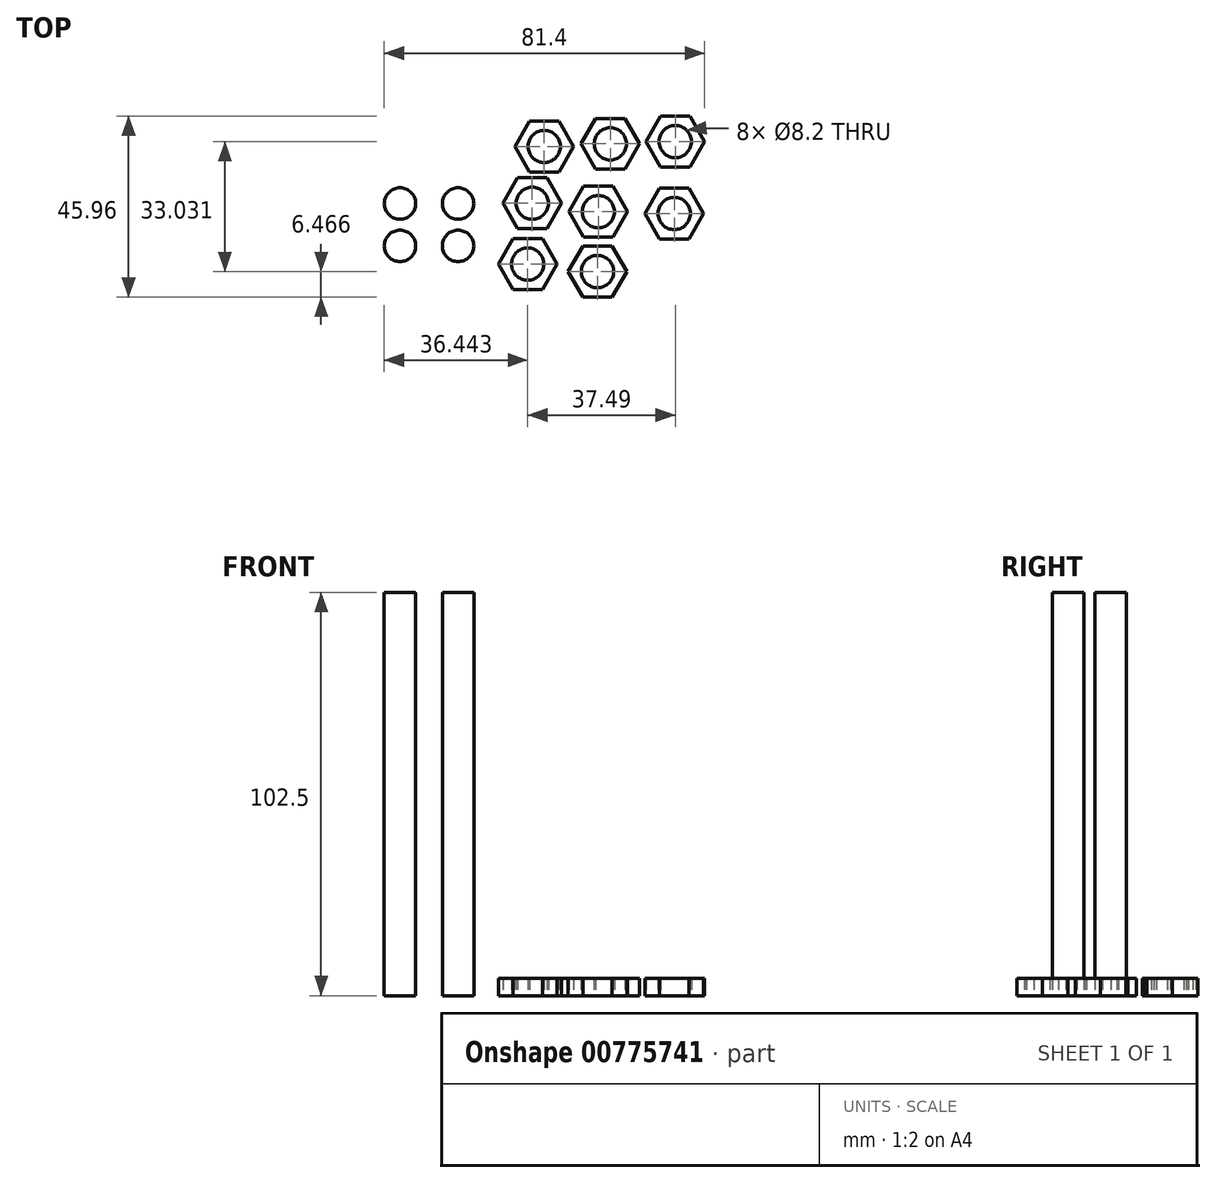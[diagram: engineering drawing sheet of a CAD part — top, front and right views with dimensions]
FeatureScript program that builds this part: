
annotation { "Feature Type Name" : "Feature", "Feature Type Description" : "" }
export const myFeature = defineFeature(function(context is Context, id is Id, definition is map)
    precondition{}
    {
        {
            var Q0;
            Q0=qCreatedBy(makeId("Top.planeOp"),FACE);
            var sketch = newSketch(context, id + "F0", { "sketchPlane" : qUnion([Q0])});
            skCircle(sketch, "E0", {"center": v(-16.12, 12.93) * mm, "radius": 4 * mm});
            skCircle(sketch, "E1", {"center": v(-1.37, 12.93) * mm, "radius": 4 * mm});
            skCircle(sketch, "E2", {"center": v(-16.12, 2.17) * mm, "radius": 4 * mm});
            skCircle(sketch, "E3", {"center": v(-1.37, 2.17) * mm, "radius": 4 * mm});
            skSolve(sketch);
        }
        {
            var Q0;
            Q0=makeQuery(id+"F0.imprint","IMPRINT",FACE,{"disambiguationData":[TD([[makeQuery(id+"F0.imprint","IMPRINT",EDGE,{"derivedFrom":sQuery(id+"F0.wireOp",EDGE,"E0")}),1.0]])]});
            var Q1;
            Q1=makeQuery(id+"F0.imprint","IMPRINT",FACE,{"disambiguationData":[TD([[makeQuery(id+"F0.imprint","IMPRINT",EDGE,{"derivedFrom":sQuery(id+"F0.wireOp",EDGE,"E1")}),1.0]])]});
            var Q2;
            Q2=makeQuery(id+"F0.imprint","IMPRINT",FACE,{"disambiguationData":[TD([[makeQuery(id+"F0.imprint","IMPRINT",EDGE,{"derivedFrom":sQuery(id+"F0.wireOp",EDGE,"E3")}),1.0]])]});
            var Q3;
            Q3=makeQuery(id+"F0.imprint","IMPRINT",FACE,{"disambiguationData":[TD([[makeQuery(id+"F0.imprint","IMPRINT",EDGE,{"derivedFrom":sQuery(id+"F0.wireOp",EDGE,"E2")}),1.0]])]});
            extrude(context, id + "F1", {"entities" : qUnion([Q0, Q1, Q2, Q3]), "depth" : 102.5 * mm, "offsetDistance" : 25.4 * mm});
        }
        {
            var Q0;
            Q0=qCreatedBy(makeId("Top.planeOp"),FACE);
            var sketch = newSketch(context, id + "F2", { "sketchPlane" : qUnion([Q0])});
            skCircle(sketch, "E4", {"center": v(16.32, -2.46) * mm, "radius": 4.1 * mm});
            skCircle(sketch, "E5.cCircle", {"center": v(16.32, -2.46) * mm, "radius": 4.1 * mm, "construction": true});
            skCircle(sketch, "E6", {"center": v(16.32, -2.46) * mm, "radius": 6.46 * mm});
            skCircle(sketch, "E7.cCircle", {"center": v(16.32, -2.46) * mm, "radius": 6.46 * mm, "construction": true});
            skLineSegment(sketch, "E7.0", {"start": v(12.6, 4) * mm, "end": v(20.05, 4) * mm});
            skLineSegment(sketch, "E7.1", {"start": v(20.05, 4) * mm, "end": v(23.79, -2.46) * mm});
            skLineSegment(sketch, "E7.2", {"start": v(23.79, -2.46) * mm, "end": v(20.05, -8.92) * mm});
            skLineSegment(sketch, "E7.3", {"start": v(20.05, -8.92) * mm, "end": v(12.6, -8.92) * mm});
            skLineSegment(sketch, "E7.4", {"start": v(12.6, -8.92) * mm, "end": v(8.86, -2.46) * mm});
            skLineSegment(sketch, "E7.5", {"start": v(8.86, -2.46) * mm, "end": v(12.6, 4) * mm});
            skPoint(sketch, "E7.0.midPoint", {"position": v(16.32, 4) * mm});
            skCircle(sketch, "E8", {"center": v(17.48, 13) * mm, "radius": 4.1 * mm});
            skCircle(sketch, "E9.cCircle", {"center": v(17.48, 13) * mm, "radius": 4.1 * mm, "construction": true});
            skCircle(sketch, "E10", {"center": v(17.48, 13) * mm, "radius": 6.46 * mm});
            skCircle(sketch, "E11.cCircle", {"center": v(17.48, 13) * mm, "radius": 6.46 * mm, "construction": true});
            skLineSegment(sketch, "E11.0", {"start": v(13.75, 19.46) * mm, "end": v(21.21, 19.46) * mm});
            skLineSegment(sketch, "E11.1", {"start": v(21.21, 19.46) * mm, "end": v(24.94, 13) * mm});
            skLineSegment(sketch, "E11.2", {"start": v(24.94, 13) * mm, "end": v(21.21, 6.53) * mm});
            skLineSegment(sketch, "E11.3", {"start": v(21.21, 6.53) * mm, "end": v(13.75, 6.53) * mm});
            skLineSegment(sketch, "E11.4", {"start": v(13.75, 6.53) * mm, "end": v(10.02, 13) * mm});
            skLineSegment(sketch, "E11.5", {"start": v(10.02, 13) * mm, "end": v(13.75, 19.46) * mm});
            skPoint(sketch, "E11.0.midPoint", {"position": v(17.48, 19.46) * mm});
            skCircle(sketch, "E12", {"center": v(20.53, 27.43) * mm, "radius": 4.1 * mm});
            skCircle(sketch, "E13.cCircle", {"center": v(20.53, 27.43) * mm, "radius": 4.1 * mm, "construction": true});
            skCircle(sketch, "E14", {"center": v(20.53, 27.43) * mm, "radius": 6.46 * mm});
            skCircle(sketch, "E15.cCircle", {"center": v(20.53, 27.43) * mm, "radius": 6.46 * mm, "construction": true});
            skLineSegment(sketch, "E15.0", {"start": v(16.8, 33.9) * mm, "end": v(24.26, 33.9) * mm});
            skLineSegment(sketch, "E15.1", {"start": v(24.26, 33.9) * mm, "end": v(27.99, 27.43) * mm});
            skLineSegment(sketch, "E15.2", {"start": v(27.99, 27.43) * mm, "end": v(24.26, 20.97) * mm});
            skLineSegment(sketch, "E15.3", {"start": v(24.26, 20.97) * mm, "end": v(16.8, 20.97) * mm});
            skLineSegment(sketch, "E15.4", {"start": v(16.8, 20.97) * mm, "end": v(13.06, 27.43) * mm});
            skLineSegment(sketch, "E15.5", {"start": v(13.06, 27.43) * mm, "end": v(16.8, 33.9) * mm});
            skPoint(sketch, "E15.0.midPoint", {"position": v(20.53, 33.9) * mm});
            skCircle(sketch, "E16", {"center": v(37.32, 28.1) * mm, "radius": 4.1 * mm});
            skCircle(sketch, "E17.cCircle", {"center": v(37.32, 28.1) * mm, "radius": 4.1 * mm, "construction": true});
            skCircle(sketch, "E18", {"center": v(37.32, 28.1) * mm, "radius": 6.46 * mm});
            skCircle(sketch, "E19.cCircle", {"center": v(37.32, 28.1) * mm, "radius": 6.46 * mm, "construction": true});
            skLineSegment(sketch, "E19.0", {"start": v(33.6, 34.57) * mm, "end": v(41.05, 34.57) * mm});
            skLineSegment(sketch, "E19.1", {"start": v(41.05, 34.57) * mm, "end": v(44.79, 28.1) * mm});
            skLineSegment(sketch, "E19.2", {"start": v(44.79, 28.1) * mm, "end": v(41.05, 21.64) * mm});
            skLineSegment(sketch, "E19.3", {"start": v(41.05, 21.64) * mm, "end": v(33.6, 21.64) * mm});
            skLineSegment(sketch, "E19.4", {"start": v(33.6, 21.64) * mm, "end": v(29.86, 28.1) * mm});
            skLineSegment(sketch, "E19.5", {"start": v(29.86, 28.1) * mm, "end": v(33.6, 34.57) * mm});
            skPoint(sketch, "E19.0.midPoint", {"position": v(37.32, 34.57) * mm});
            skCircle(sketch, "E20", {"center": v(53.81, 28.67) * mm, "radius": 4.1 * mm});
            skCircle(sketch, "E21.cCircle", {"center": v(53.81, 28.67) * mm, "radius": 4.1 * mm, "construction": true});
            skCircle(sketch, "E22", {"center": v(53.81, 28.67) * mm, "radius": 6.46 * mm});
            skCircle(sketch, "E23.cCircle", {"center": v(53.81, 28.67) * mm, "radius": 6.46 * mm, "construction": true});
            skLineSegment(sketch, "E23.0", {"start": v(50.08, 35.13) * mm, "end": v(57.54, 35.13) * mm});
            skLineSegment(sketch, "E23.1", {"start": v(57.54, 35.13) * mm, "end": v(61.28, 28.67) * mm});
            skLineSegment(sketch, "E23.2", {"start": v(61.28, 28.67) * mm, "end": v(57.54, 22.2) * mm});
            skLineSegment(sketch, "E23.3", {"start": v(57.54, 22.2) * mm, "end": v(50.08, 22.2) * mm});
            skLineSegment(sketch, "E23.4", {"start": v(50.08, 22.2) * mm, "end": v(46.35, 28.67) * mm});
            skLineSegment(sketch, "E23.5", {"start": v(46.35, 28.67) * mm, "end": v(50.08, 35.13) * mm});
            skPoint(sketch, "E23.0.midPoint", {"position": v(53.81, 35.13) * mm});
            skCircle(sketch, "E24", {"center": v(34.28, 10.86) * mm, "radius": 4.1 * mm});
            skCircle(sketch, "E25.cCircle", {"center": v(34.28, 10.86) * mm, "radius": 4.1 * mm, "construction": true});
            skCircle(sketch, "E26", {"center": v(34.28, 10.86) * mm, "radius": 6.46 * mm});
            skCircle(sketch, "E27.cCircle", {"center": v(34.28, 10.86) * mm, "radius": 6.46 * mm, "construction": true});
            skLineSegment(sketch, "E27.0", {"start": v(30.55, 17.32) * mm, "end": v(38.01, 17.32) * mm});
            skLineSegment(sketch, "E27.1", {"start": v(38.01, 17.32) * mm, "end": v(41.74, 10.86) * mm});
            skLineSegment(sketch, "E27.2", {"start": v(41.74, 10.86) * mm, "end": v(38.01, 4.4) * mm});
            skLineSegment(sketch, "E27.3", {"start": v(38.01, 4.4) * mm, "end": v(30.55, 4.4) * mm});
            skLineSegment(sketch, "E27.4", {"start": v(30.55, 4.4) * mm, "end": v(26.82, 10.86) * mm});
            skLineSegment(sketch, "E27.5", {"start": v(26.82, 10.86) * mm, "end": v(30.55, 17.32) * mm});
            skPoint(sketch, "E27.0.midPoint", {"position": v(34.28, 17.32) * mm});
            skCircle(sketch, "E28", {"center": v(53.56, 10.4) * mm, "radius": 4.1 * mm});
            skCircle(sketch, "E29.cCircle", {"center": v(53.56, 10.4) * mm, "radius": 4.1 * mm, "construction": true});
            skCircle(sketch, "E30", {"center": v(53.56, 10.4) * mm, "radius": 6.46 * mm});
            skCircle(sketch, "E31.cCircle", {"center": v(53.56, 10.4) * mm, "radius": 6.46 * mm, "construction": true});
            skLineSegment(sketch, "E31.0", {"start": v(49.83, 16.87) * mm, "end": v(57.29, 16.87) * mm});
            skLineSegment(sketch, "E31.1", {"start": v(57.29, 16.87) * mm, "end": v(61.02, 10.4) * mm});
            skLineSegment(sketch, "E31.2", {"start": v(61.02, 10.4) * mm, "end": v(57.29, 3.94) * mm});
            skLineSegment(sketch, "E31.3", {"start": v(57.29, 3.94) * mm, "end": v(49.83, 3.94) * mm});
            skLineSegment(sketch, "E31.4", {"start": v(49.83, 3.94) * mm, "end": v(46.1, 10.4) * mm});
            skLineSegment(sketch, "E31.5", {"start": v(46.1, 10.4) * mm, "end": v(49.83, 16.87) * mm});
            skPoint(sketch, "E31.0.midPoint", {"position": v(53.56, 16.87) * mm});
            skCircle(sketch, "E32", {"center": v(34.05, -4.36) * mm, "radius": 4.1 * mm});
            skCircle(sketch, "E33.cCircle", {"center": v(34.05, -4.36) * mm, "radius": 4.1 * mm, "construction": true});
            skCircle(sketch, "E34", {"center": v(34.05, -4.36) * mm, "radius": 6.46 * mm});
            skCircle(sketch, "E35.cCircle", {"center": v(34.05, -4.36) * mm, "radius": 6.46 * mm, "construction": true});
            skLineSegment(sketch, "E35.0", {"start": v(30.32, 2.1) * mm, "end": v(37.78, 2.1) * mm});
            skLineSegment(sketch, "E35.1", {"start": v(37.78, 2.1) * mm, "end": v(41.52, -4.36) * mm});
            skLineSegment(sketch, "E35.2", {"start": v(41.52, -4.36) * mm, "end": v(37.78, -10.83) * mm});
            skLineSegment(sketch, "E35.3", {"start": v(37.78, -10.83) * mm, "end": v(30.32, -10.83) * mm});
            skLineSegment(sketch, "E35.4", {"start": v(30.32, -10.83) * mm, "end": v(26.6, -4.36) * mm});
            skLineSegment(sketch, "E35.5", {"start": v(26.6, -4.36) * mm, "end": v(30.32, 2.1) * mm});
            skPoint(sketch, "E35.0.midPoint", {"position": v(34.05, 2.1) * mm});
            skSolve(sketch);
        }
        {
            var Q0;
            Q0=makeQuery(id+"F2.imprint","IMPRINT",FACE,{"disambiguationData":[TD([[makeQuery(id+"F2.imprint","IMPRINT",EDGE,{"derivedFrom":sQuery(id+"F2.wireOp",EDGE,"E12")}),-1.0]])]});
            var Q1;
            {var subQ0=sQuery(id+"F2.wireOp",EDGE,"E15.3");var subQ1=sQuery(id+"F2.wireOp",EDGE,"E14");var subQ2=makeQuery(id+"F2.imprint","INTERSECT",VERTEX,{"derivedFrom":[subQ1,subQ0]});Q1=makeQuery(id+"F2.imprint","IMPRINT",FACE,{"disambiguationData":[TD([[makeQuery(id+"F2.imprint","IMPRINT",EDGE,{"disambiguationData":[TD([[subQ2,-1.0]])],"derivedFrom":subQ1}),-1.0]])]});}
            var Q2;
            {var subQ0=sQuery(id+"F2.wireOp",EDGE,"E15.1");var subQ1=sQuery(id+"F2.wireOp",EDGE,"E14");var subQ2=makeQuery(id+"F2.imprint","INTERSECT",VERTEX,{"derivedFrom":[subQ1,subQ0]});Q2=makeQuery(id+"F2.imprint","IMPRINT",FACE,{"disambiguationData":[TD([[makeQuery(id+"F2.imprint","IMPRINT",EDGE,{"disambiguationData":[TD([[subQ2,1.0]])],"derivedFrom":subQ1}),-1.0]])]});}
            var Q3;
            {var subQ0=sQuery(id+"F2.wireOp",EDGE,"E15.0");var subQ1=sQuery(id+"F2.wireOp",EDGE,"E14");var subQ2=makeQuery(id+"F2.imprint","INTERSECT",VERTEX,{"derivedFrom":[subQ1,subQ0]});Q3=makeQuery(id+"F2.imprint","IMPRINT",FACE,{"disambiguationData":[TD([[makeQuery(id+"F2.imprint","IMPRINT",EDGE,{"disambiguationData":[TD([[subQ2,1.0]])],"derivedFrom":subQ1}),-1.0]])]});}
            var Q4;
            {var subQ0=sQuery(id+"F2.wireOp",EDGE,"E15.0");var subQ1=sQuery(id+"F2.wireOp",EDGE,"E14");var subQ2=makeQuery(id+"F2.imprint","INTERSECT",VERTEX,{"derivedFrom":[subQ1,subQ0]});Q4=makeQuery(id+"F2.imprint","IMPRINT",FACE,{"disambiguationData":[TD([[makeQuery(id+"F2.imprint","IMPRINT",EDGE,{"disambiguationData":[TD([[subQ2,-1.0]])],"derivedFrom":subQ1}),-1.0]])]});}
            var Q5;
            {var subQ0=sQuery(id+"F2.wireOp",EDGE,"E15.5");var subQ1=sQuery(id+"F2.wireOp",EDGE,"E14");var subQ2=makeQuery(id+"F2.imprint","INTERSECT",VERTEX,{"derivedFrom":[subQ1,subQ0]});Q5=makeQuery(id+"F2.imprint","IMPRINT",FACE,{"disambiguationData":[TD([[makeQuery(id+"F2.imprint","IMPRINT",EDGE,{"disambiguationData":[TD([[subQ2,-1.0]])],"derivedFrom":subQ1}),-1.0]])]});}
            var Q6;
            {var subQ0=sQuery(id+"F2.wireOp",EDGE,"E15.4");var subQ1=sQuery(id+"F2.wireOp",EDGE,"E14");var subQ2=makeQuery(id+"F2.imprint","INTERSECT",VERTEX,{"derivedFrom":[subQ1,subQ0]});Q6=makeQuery(id+"F2.imprint","IMPRINT",FACE,{"disambiguationData":[TD([[makeQuery(id+"F2.imprint","IMPRINT",EDGE,{"disambiguationData":[TD([[subQ2,-1.0]])],"derivedFrom":subQ1}),-1.0]])]});}
            var Q7;
            Q7=makeQuery(id+"F2.imprint","IMPRINT",FACE,{"disambiguationData":[TD([[makeQuery(id+"F2.imprint","IMPRINT",EDGE,{"derivedFrom":sQuery(id+"F2.wireOp",EDGE,"E8")}),-1.0]])]});
            var Q8;
            {var subQ0=sQuery(id+"F2.wireOp",EDGE,"E11.0");var subQ1=sQuery(id+"F2.wireOp",EDGE,"E10");var subQ2=makeQuery(id+"F2.imprint","INTERSECT",VERTEX,{"derivedFrom":[subQ1,subQ0]});Q8=makeQuery(id+"F2.imprint","IMPRINT",FACE,{"disambiguationData":[TD([[makeQuery(id+"F2.imprint","IMPRINT",EDGE,{"disambiguationData":[TD([[subQ2,1.0]])],"derivedFrom":subQ1}),-1.0]])]});}
            var Q9;
            {var subQ0=sQuery(id+"F2.wireOp",EDGE,"E11.1");var subQ1=sQuery(id+"F2.wireOp",EDGE,"E10");var subQ2=makeQuery(id+"F2.imprint","INTERSECT",VERTEX,{"derivedFrom":[subQ1,subQ0]});Q9=makeQuery(id+"F2.imprint","IMPRINT",FACE,{"disambiguationData":[TD([[makeQuery(id+"F2.imprint","IMPRINT",EDGE,{"disambiguationData":[TD([[subQ2,1.0]])],"derivedFrom":subQ1}),-1.0]])]});}
            var Q10;
            {var subQ0=sQuery(id+"F2.wireOp",EDGE,"E11.3");var subQ1=sQuery(id+"F2.wireOp",EDGE,"E10");var subQ2=makeQuery(id+"F2.imprint","INTERSECT",VERTEX,{"derivedFrom":[subQ1,subQ0]});Q10=makeQuery(id+"F2.imprint","IMPRINT",FACE,{"disambiguationData":[TD([[makeQuery(id+"F2.imprint","IMPRINT",EDGE,{"disambiguationData":[TD([[subQ2,-1.0]])],"derivedFrom":subQ1}),-1.0]])]});}
            var Q11;
            {var subQ0=sQuery(id+"F2.wireOp",EDGE,"E11.4");var subQ1=sQuery(id+"F2.wireOp",EDGE,"E10");var subQ2=makeQuery(id+"F2.imprint","INTERSECT",VERTEX,{"derivedFrom":[subQ1,subQ0]});Q11=makeQuery(id+"F2.imprint","IMPRINT",FACE,{"disambiguationData":[TD([[makeQuery(id+"F2.imprint","IMPRINT",EDGE,{"disambiguationData":[TD([[subQ2,-1.0]])],"derivedFrom":subQ1}),-1.0]])]});}
            var Q12;
            {var subQ0=sQuery(id+"F2.wireOp",EDGE,"E11.5");var subQ1=sQuery(id+"F2.wireOp",EDGE,"E10");var subQ2=makeQuery(id+"F2.imprint","INTERSECT",VERTEX,{"derivedFrom":[subQ1,subQ0]});Q12=makeQuery(id+"F2.imprint","IMPRINT",FACE,{"disambiguationData":[TD([[makeQuery(id+"F2.imprint","IMPRINT",EDGE,{"disambiguationData":[TD([[subQ2,-1.0]])],"derivedFrom":subQ1}),-1.0]])]});}
            var Q13;
            {var subQ0=sQuery(id+"F2.wireOp",EDGE,"E11.0");var subQ1=sQuery(id+"F2.wireOp",EDGE,"E10");var subQ2=makeQuery(id+"F2.imprint","INTERSECT",VERTEX,{"derivedFrom":[subQ1,subQ0]});Q13=makeQuery(id+"F2.imprint","IMPRINT",FACE,{"disambiguationData":[TD([[makeQuery(id+"F2.imprint","IMPRINT",EDGE,{"disambiguationData":[TD([[subQ2,-1.0]])],"derivedFrom":subQ1}),-1.0]])]});}
            var Q14;
            {var subQ0=sQuery(id+"F2.wireOp",EDGE,"E19.0");var subQ1=sQuery(id+"F2.wireOp",EDGE,"E18");var subQ2=makeQuery(id+"F2.imprint","INTERSECT",VERTEX,{"derivedFrom":[subQ1,subQ0]});Q14=makeQuery(id+"F2.imprint","IMPRINT",FACE,{"disambiguationData":[TD([[makeQuery(id+"F2.imprint","IMPRINT",EDGE,{"disambiguationData":[TD([[subQ2,-1.0]])],"derivedFrom":subQ1}),-1.0]])]});}
            var Q15;
            Q15=makeQuery(id+"F2.imprint","IMPRINT",FACE,{"disambiguationData":[TD([[makeQuery(id+"F2.imprint","IMPRINT",EDGE,{"derivedFrom":sQuery(id+"F2.wireOp",EDGE,"E16")}),-1.0]])]});
            var Q16;
            {var subQ0=sQuery(id+"F2.wireOp",EDGE,"E19.5");var subQ1=sQuery(id+"F2.wireOp",EDGE,"E18");var subQ2=makeQuery(id+"F2.imprint","INTERSECT",VERTEX,{"derivedFrom":[subQ1,subQ0]});Q16=makeQuery(id+"F2.imprint","IMPRINT",FACE,{"disambiguationData":[TD([[makeQuery(id+"F2.imprint","IMPRINT",EDGE,{"disambiguationData":[TD([[subQ2,-1.0]])],"derivedFrom":subQ1}),-1.0]])]});}
            var Q17;
            {var subQ0=sQuery(id+"F2.wireOp",EDGE,"E19.4");var subQ1=sQuery(id+"F2.wireOp",EDGE,"E18");var subQ2=makeQuery(id+"F2.imprint","INTERSECT",VERTEX,{"derivedFrom":[subQ1,subQ0]});Q17=makeQuery(id+"F2.imprint","IMPRINT",FACE,{"disambiguationData":[TD([[makeQuery(id+"F2.imprint","IMPRINT",EDGE,{"disambiguationData":[TD([[subQ2,-1.0]])],"derivedFrom":subQ1}),-1.0]])]});}
            var Q18;
            {var subQ0=sQuery(id+"F2.wireOp",EDGE,"E19.3");var subQ1=sQuery(id+"F2.wireOp",EDGE,"E18");var subQ2=makeQuery(id+"F2.imprint","INTERSECT",VERTEX,{"derivedFrom":[subQ1,subQ0]});Q18=makeQuery(id+"F2.imprint","IMPRINT",FACE,{"disambiguationData":[TD([[makeQuery(id+"F2.imprint","IMPRINT",EDGE,{"disambiguationData":[TD([[subQ2,-1.0]])],"derivedFrom":subQ1}),-1.0]])]});}
            var Q19;
            {var subQ0=sQuery(id+"F2.wireOp",EDGE,"E19.1");var subQ1=sQuery(id+"F2.wireOp",EDGE,"E18");var subQ2=makeQuery(id+"F2.imprint","INTERSECT",VERTEX,{"derivedFrom":[subQ1,subQ0]});Q19=makeQuery(id+"F2.imprint","IMPRINT",FACE,{"disambiguationData":[TD([[makeQuery(id+"F2.imprint","IMPRINT",EDGE,{"disambiguationData":[TD([[subQ2,1.0]])],"derivedFrom":subQ1}),-1.0]])]});}
            var Q20;
            {var subQ0=sQuery(id+"F2.wireOp",EDGE,"E19.0");var subQ1=sQuery(id+"F2.wireOp",EDGE,"E18");var subQ2=makeQuery(id+"F2.imprint","INTERSECT",VERTEX,{"derivedFrom":[subQ1,subQ0]});Q20=makeQuery(id+"F2.imprint","IMPRINT",FACE,{"disambiguationData":[TD([[makeQuery(id+"F2.imprint","IMPRINT",EDGE,{"disambiguationData":[TD([[subQ2,1.0]])],"derivedFrom":subQ1}),-1.0]])]});}
            var Q21;
            {var subQ0=sQuery(id+"F2.wireOp",EDGE,"E23.0");var subQ1=sQuery(id+"F2.wireOp",EDGE,"E22");var subQ2=makeQuery(id+"F2.imprint","INTERSECT",VERTEX,{"derivedFrom":[subQ1,subQ0]});Q21=makeQuery(id+"F2.imprint","IMPRINT",FACE,{"disambiguationData":[TD([[makeQuery(id+"F2.imprint","IMPRINT",EDGE,{"disambiguationData":[TD([[subQ2,-1.0]])],"derivedFrom":subQ1}),-1.0]])]});}
            var Q22;
            Q22=makeQuery(id+"F2.imprint","IMPRINT",FACE,{"disambiguationData":[TD([[makeQuery(id+"F2.imprint","IMPRINT",EDGE,{"derivedFrom":sQuery(id+"F2.wireOp",EDGE,"E20")}),-1.0]])]});
            var Q23;
            {var subQ0=sQuery(id+"F2.wireOp",EDGE,"E23.5");var subQ1=sQuery(id+"F2.wireOp",EDGE,"E22");var subQ2=makeQuery(id+"F2.imprint","INTERSECT",VERTEX,{"derivedFrom":[subQ1,subQ0]});Q23=makeQuery(id+"F2.imprint","IMPRINT",FACE,{"disambiguationData":[TD([[makeQuery(id+"F2.imprint","IMPRINT",EDGE,{"disambiguationData":[TD([[subQ2,-1.0]])],"derivedFrom":subQ1}),-1.0]])]});}
            var Q24;
            {var subQ0=sQuery(id+"F2.wireOp",EDGE,"E23.4");var subQ1=sQuery(id+"F2.wireOp",EDGE,"E22");var subQ2=makeQuery(id+"F2.imprint","INTERSECT",VERTEX,{"derivedFrom":[subQ1,subQ0]});Q24=makeQuery(id+"F2.imprint","IMPRINT",FACE,{"disambiguationData":[TD([[makeQuery(id+"F2.imprint","IMPRINT",EDGE,{"disambiguationData":[TD([[subQ2,-1.0]])],"derivedFrom":subQ1}),-1.0]])]});}
            var Q25;
            {var subQ0=sQuery(id+"F2.wireOp",EDGE,"E23.3");var subQ1=sQuery(id+"F2.wireOp",EDGE,"E22");var subQ2=makeQuery(id+"F2.imprint","INTERSECT",VERTEX,{"derivedFrom":[subQ1,subQ0]});Q25=makeQuery(id+"F2.imprint","IMPRINT",FACE,{"disambiguationData":[TD([[makeQuery(id+"F2.imprint","IMPRINT",EDGE,{"disambiguationData":[TD([[subQ2,-1.0]])],"derivedFrom":subQ1}),-1.0]])]});}
            var Q26;
            {var subQ0=sQuery(id+"F2.wireOp",EDGE,"E23.1");var subQ1=sQuery(id+"F2.wireOp",EDGE,"E22");var subQ2=makeQuery(id+"F2.imprint","INTERSECT",VERTEX,{"derivedFrom":[subQ1,subQ0]});Q26=makeQuery(id+"F2.imprint","IMPRINT",FACE,{"disambiguationData":[TD([[makeQuery(id+"F2.imprint","IMPRINT",EDGE,{"disambiguationData":[TD([[subQ2,1.0]])],"derivedFrom":subQ1}),-1.0]])]});}
            var Q27;
            {var subQ0=sQuery(id+"F2.wireOp",EDGE,"E23.0");var subQ1=sQuery(id+"F2.wireOp",EDGE,"E22");var subQ2=makeQuery(id+"F2.imprint","INTERSECT",VERTEX,{"derivedFrom":[subQ1,subQ0]});Q27=makeQuery(id+"F2.imprint","IMPRINT",FACE,{"disambiguationData":[TD([[makeQuery(id+"F2.imprint","IMPRINT",EDGE,{"disambiguationData":[TD([[subQ2,1.0]])],"derivedFrom":subQ1}),-1.0]])]});}
            var Q28;
            Q28=makeQuery(id+"F2.imprint","IMPRINT",FACE,{"disambiguationData":[TD([[makeQuery(id+"F2.imprint","IMPRINT",EDGE,{"derivedFrom":sQuery(id+"F2.wireOp",EDGE,"E28")}),-1.0]])]});
            var Q29;
            Q29=makeQuery(id+"F2.imprint","IMPRINT",FACE,{"disambiguationData":[TD([[makeQuery(id+"F2.imprint","IMPRINT",EDGE,{"derivedFrom":sQuery(id+"F2.wireOp",EDGE,"E24")}),-1.0]])]});
            var Q30;
            Q30=makeQuery(id+"F2.imprint","IMPRINT",FACE,{"disambiguationData":[TD([[makeQuery(id+"F2.imprint","IMPRINT",EDGE,{"derivedFrom":sQuery(id+"F2.wireOp",EDGE,"E4")}),-1.0]])]});
            var Q31;
            Q31=makeQuery(id+"F2.imprint","IMPRINT",FACE,{"disambiguationData":[TD([[makeQuery(id+"F2.imprint","IMPRINT",EDGE,{"derivedFrom":sQuery(id+"F2.wireOp",EDGE,"E32")}),-1.0]])]});
            var Q32;
            {var subQ0=sQuery(id+"F2.wireOp",EDGE,"E27.0");var subQ1=sQuery(id+"F2.wireOp",EDGE,"E26");var subQ2=makeQuery(id+"F2.imprint","INTERSECT",VERTEX,{"derivedFrom":[subQ1,subQ0]});Q32=makeQuery(id+"F2.imprint","IMPRINT",FACE,{"disambiguationData":[TD([[makeQuery(id+"F2.imprint","IMPRINT",EDGE,{"disambiguationData":[TD([[subQ2,-1.0]])],"derivedFrom":subQ1}),-1.0]])]});}
            var Q33;
            {var subQ0=sQuery(id+"F2.wireOp",EDGE,"E27.5");var subQ1=sQuery(id+"F2.wireOp",EDGE,"E26");var subQ2=makeQuery(id+"F2.imprint","INTERSECT",VERTEX,{"derivedFrom":[subQ1,subQ0]});Q33=makeQuery(id+"F2.imprint","IMPRINT",FACE,{"disambiguationData":[TD([[makeQuery(id+"F2.imprint","IMPRINT",EDGE,{"disambiguationData":[TD([[subQ2,-1.0]])],"derivedFrom":subQ1}),-1.0]])]});}
            var Q34;
            {var subQ0=sQuery(id+"F2.wireOp",EDGE,"E27.4");var subQ1=sQuery(id+"F2.wireOp",EDGE,"E26");var subQ2=makeQuery(id+"F2.imprint","INTERSECT",VERTEX,{"derivedFrom":[subQ1,subQ0]});Q34=makeQuery(id+"F2.imprint","IMPRINT",FACE,{"disambiguationData":[TD([[makeQuery(id+"F2.imprint","IMPRINT",EDGE,{"disambiguationData":[TD([[subQ2,-1.0]])],"derivedFrom":subQ1}),-1.0]])]});}
            var Q35;
            {var subQ0=sQuery(id+"F2.wireOp",EDGE,"E27.3");var subQ1=sQuery(id+"F2.wireOp",EDGE,"E26");var subQ2=makeQuery(id+"F2.imprint","INTERSECT",VERTEX,{"derivedFrom":[subQ1,subQ0]});Q35=makeQuery(id+"F2.imprint","IMPRINT",FACE,{"disambiguationData":[TD([[makeQuery(id+"F2.imprint","IMPRINT",EDGE,{"disambiguationData":[TD([[subQ2,-1.0]])],"derivedFrom":subQ1}),-1.0]])]});}
            var Q36;
            {var subQ0=sQuery(id+"F2.wireOp",EDGE,"E27.1");var subQ1=sQuery(id+"F2.wireOp",EDGE,"E26");var subQ2=makeQuery(id+"F2.imprint","INTERSECT",VERTEX,{"derivedFrom":[subQ1,subQ0]});Q36=makeQuery(id+"F2.imprint","IMPRINT",FACE,{"disambiguationData":[TD([[makeQuery(id+"F2.imprint","IMPRINT",EDGE,{"disambiguationData":[TD([[subQ2,1.0]])],"derivedFrom":subQ1}),-1.0]])]});}
            var Q37;
            {var subQ0=sQuery(id+"F2.wireOp",EDGE,"E27.0");var subQ1=sQuery(id+"F2.wireOp",EDGE,"E26");var subQ2=makeQuery(id+"F2.imprint","INTERSECT",VERTEX,{"derivedFrom":[subQ1,subQ0]});Q37=makeQuery(id+"F2.imprint","IMPRINT",FACE,{"disambiguationData":[TD([[makeQuery(id+"F2.imprint","IMPRINT",EDGE,{"disambiguationData":[TD([[subQ2,1.0]])],"derivedFrom":subQ1}),-1.0]])]});}
            var Q38;
            {var subQ0=sQuery(id+"F2.wireOp",EDGE,"E31.0");var subQ1=sQuery(id+"F2.wireOp",EDGE,"E30");var subQ2=makeQuery(id+"F2.imprint","INTERSECT",VERTEX,{"derivedFrom":[subQ1,subQ0]});Q38=makeQuery(id+"F2.imprint","IMPRINT",FACE,{"disambiguationData":[TD([[makeQuery(id+"F2.imprint","IMPRINT",EDGE,{"disambiguationData":[TD([[subQ2,-1.0]])],"derivedFrom":subQ1}),-1.0]])]});}
            var Q39;
            {var subQ0=sQuery(id+"F2.wireOp",EDGE,"E31.5");var subQ1=sQuery(id+"F2.wireOp",EDGE,"E30");var subQ2=makeQuery(id+"F2.imprint","INTERSECT",VERTEX,{"derivedFrom":[subQ1,subQ0]});Q39=makeQuery(id+"F2.imprint","IMPRINT",FACE,{"disambiguationData":[TD([[makeQuery(id+"F2.imprint","IMPRINT",EDGE,{"disambiguationData":[TD([[subQ2,-1.0]])],"derivedFrom":subQ1}),-1.0]])]});}
            var Q40;
            {var subQ0=sQuery(id+"F2.wireOp",EDGE,"E31.4");var subQ1=sQuery(id+"F2.wireOp",EDGE,"E30");var subQ2=makeQuery(id+"F2.imprint","INTERSECT",VERTEX,{"derivedFrom":[subQ1,subQ0]});Q40=makeQuery(id+"F2.imprint","IMPRINT",FACE,{"disambiguationData":[TD([[makeQuery(id+"F2.imprint","IMPRINT",EDGE,{"disambiguationData":[TD([[subQ2,-1.0]])],"derivedFrom":subQ1}),-1.0]])]});}
            var Q41;
            {var subQ0=sQuery(id+"F2.wireOp",EDGE,"E31.3");var subQ1=sQuery(id+"F2.wireOp",EDGE,"E30");var subQ2=makeQuery(id+"F2.imprint","INTERSECT",VERTEX,{"derivedFrom":[subQ1,subQ0]});Q41=makeQuery(id+"F2.imprint","IMPRINT",FACE,{"disambiguationData":[TD([[makeQuery(id+"F2.imprint","IMPRINT",EDGE,{"disambiguationData":[TD([[subQ2,-1.0]])],"derivedFrom":subQ1}),-1.0]])]});}
            var Q42;
            {var subQ0=sQuery(id+"F2.wireOp",EDGE,"E31.1");var subQ1=sQuery(id+"F2.wireOp",EDGE,"E30");var subQ2=makeQuery(id+"F2.imprint","INTERSECT",VERTEX,{"derivedFrom":[subQ1,subQ0]});Q42=makeQuery(id+"F2.imprint","IMPRINT",FACE,{"disambiguationData":[TD([[makeQuery(id+"F2.imprint","IMPRINT",EDGE,{"disambiguationData":[TD([[subQ2,1.0]])],"derivedFrom":subQ1}),-1.0]])]});}
            var Q43;
            {var subQ0=sQuery(id+"F2.wireOp",EDGE,"E31.0");var subQ1=sQuery(id+"F2.wireOp",EDGE,"E30");var subQ2=makeQuery(id+"F2.imprint","INTERSECT",VERTEX,{"derivedFrom":[subQ1,subQ0]});Q43=makeQuery(id+"F2.imprint","IMPRINT",FACE,{"disambiguationData":[TD([[makeQuery(id+"F2.imprint","IMPRINT",EDGE,{"disambiguationData":[TD([[subQ2,1.0]])],"derivedFrom":subQ1}),-1.0]])]});}
            var Q44;
            {var subQ0=sQuery(id+"F2.wireOp",EDGE,"E35.0");var subQ1=sQuery(id+"F2.wireOp",EDGE,"E34");var subQ2=makeQuery(id+"F2.imprint","INTERSECT",VERTEX,{"derivedFrom":[subQ1,subQ0]});Q44=makeQuery(id+"F2.imprint","IMPRINT",FACE,{"disambiguationData":[TD([[makeQuery(id+"F2.imprint","IMPRINT",EDGE,{"disambiguationData":[TD([[subQ2,1.0]])],"derivedFrom":subQ1}),-1.0]])]});}
            var Q45;
            {var subQ0=sQuery(id+"F2.wireOp",EDGE,"E35.1");var subQ1=sQuery(id+"F2.wireOp",EDGE,"E34");var subQ2=makeQuery(id+"F2.imprint","INTERSECT",VERTEX,{"derivedFrom":[subQ1,subQ0]});Q45=makeQuery(id+"F2.imprint","IMPRINT",FACE,{"disambiguationData":[TD([[makeQuery(id+"F2.imprint","IMPRINT",EDGE,{"disambiguationData":[TD([[subQ2,1.0]])],"derivedFrom":subQ1}),-1.0]])]});}
            var Q46;
            {var subQ0=sQuery(id+"F2.wireOp",EDGE,"E35.3");var subQ1=sQuery(id+"F2.wireOp",EDGE,"E34");var subQ2=makeQuery(id+"F2.imprint","INTERSECT",VERTEX,{"derivedFrom":[subQ1,subQ0]});Q46=makeQuery(id+"F2.imprint","IMPRINT",FACE,{"disambiguationData":[TD([[makeQuery(id+"F2.imprint","IMPRINT",EDGE,{"disambiguationData":[TD([[subQ2,-1.0]])],"derivedFrom":subQ1}),-1.0]])]});}
            var Q47;
            {var subQ0=sQuery(id+"F2.wireOp",EDGE,"E35.4");var subQ1=sQuery(id+"F2.wireOp",EDGE,"E34");var subQ2=makeQuery(id+"F2.imprint","INTERSECT",VERTEX,{"derivedFrom":[subQ1,subQ0]});Q47=makeQuery(id+"F2.imprint","IMPRINT",FACE,{"disambiguationData":[TD([[makeQuery(id+"F2.imprint","IMPRINT",EDGE,{"disambiguationData":[TD([[subQ2,-1.0]])],"derivedFrom":subQ1}),-1.0]])]});}
            var Q48;
            {var subQ0=sQuery(id+"F2.wireOp",EDGE,"E35.5");var subQ1=sQuery(id+"F2.wireOp",EDGE,"E34");var subQ2=makeQuery(id+"F2.imprint","INTERSECT",VERTEX,{"derivedFrom":[subQ1,subQ0]});Q48=makeQuery(id+"F2.imprint","IMPRINT",FACE,{"disambiguationData":[TD([[makeQuery(id+"F2.imprint","IMPRINT",EDGE,{"disambiguationData":[TD([[subQ2,-1.0]])],"derivedFrom":subQ1}),-1.0]])]});}
            var Q49;
            {var subQ0=sQuery(id+"F2.wireOp",EDGE,"E35.0");var subQ1=sQuery(id+"F2.wireOp",EDGE,"E34");var subQ2=makeQuery(id+"F2.imprint","INTERSECT",VERTEX,{"derivedFrom":[subQ1,subQ0]});Q49=makeQuery(id+"F2.imprint","IMPRINT",FACE,{"disambiguationData":[TD([[makeQuery(id+"F2.imprint","IMPRINT",EDGE,{"disambiguationData":[TD([[subQ2,-1.0]])],"derivedFrom":subQ1}),-1.0]])]});}
            var Q50;
            {var subQ0=sQuery(id+"F2.wireOp",EDGE,"E7.0");var subQ1=sQuery(id+"F2.wireOp",EDGE,"E6");var subQ2=makeQuery(id+"F2.imprint","INTERSECT",VERTEX,{"derivedFrom":[subQ1,subQ0]});Q50=makeQuery(id+"F2.imprint","IMPRINT",FACE,{"disambiguationData":[TD([[makeQuery(id+"F2.imprint","IMPRINT",EDGE,{"disambiguationData":[TD([[subQ2,1.0]])],"derivedFrom":subQ1}),-1.0]])]});}
            var Q51;
            {var subQ0=sQuery(id+"F2.wireOp",EDGE,"E7.0");var subQ1=sQuery(id+"F2.wireOp",EDGE,"E6");var subQ2=makeQuery(id+"F2.imprint","INTERSECT",VERTEX,{"derivedFrom":[subQ1,subQ0]});Q51=makeQuery(id+"F2.imprint","IMPRINT",FACE,{"disambiguationData":[TD([[makeQuery(id+"F2.imprint","IMPRINT",EDGE,{"disambiguationData":[TD([[subQ2,-1.0]])],"derivedFrom":subQ1}),-1.0]])]});}
            var Q52;
            {var subQ0=sQuery(id+"F2.wireOp",EDGE,"E7.5");var subQ1=sQuery(id+"F2.wireOp",EDGE,"E6");var subQ2=makeQuery(id+"F2.imprint","INTERSECT",VERTEX,{"derivedFrom":[subQ1,subQ0]});Q52=makeQuery(id+"F2.imprint","IMPRINT",FACE,{"disambiguationData":[TD([[makeQuery(id+"F2.imprint","IMPRINT",EDGE,{"disambiguationData":[TD([[subQ2,-1.0]])],"derivedFrom":subQ1}),-1.0]])]});}
            var Q53;
            {var subQ0=sQuery(id+"F2.wireOp",EDGE,"E7.4");var subQ1=sQuery(id+"F2.wireOp",EDGE,"E6");var subQ2=makeQuery(id+"F2.imprint","INTERSECT",VERTEX,{"derivedFrom":[subQ1,subQ0]});Q53=makeQuery(id+"F2.imprint","IMPRINT",FACE,{"disambiguationData":[TD([[makeQuery(id+"F2.imprint","IMPRINT",EDGE,{"disambiguationData":[TD([[subQ2,-1.0]])],"derivedFrom":subQ1}),-1.0]])]});}
            var Q54;
            {var subQ0=sQuery(id+"F2.wireOp",EDGE,"E7.3");var subQ1=sQuery(id+"F2.wireOp",EDGE,"E6");var subQ2=makeQuery(id+"F2.imprint","INTERSECT",VERTEX,{"derivedFrom":[subQ1,subQ0]});Q54=makeQuery(id+"F2.imprint","IMPRINT",FACE,{"disambiguationData":[TD([[makeQuery(id+"F2.imprint","IMPRINT",EDGE,{"disambiguationData":[TD([[subQ2,-1.0]])],"derivedFrom":subQ1}),-1.0]])]});}
            var Q55;
            {var subQ0=sQuery(id+"F2.wireOp",EDGE,"E7.1");var subQ1=sQuery(id+"F2.wireOp",EDGE,"E6");var subQ2=makeQuery(id+"F2.imprint","INTERSECT",VERTEX,{"derivedFrom":[subQ1,subQ0]});Q55=makeQuery(id+"F2.imprint","IMPRINT",FACE,{"disambiguationData":[TD([[makeQuery(id+"F2.imprint","IMPRINT",EDGE,{"disambiguationData":[TD([[subQ2,1.0]])],"derivedFrom":subQ1}),-1.0]])]});}
            extrude(context, id + "F3", {"entities" : qUnion([Q0, Q1, Q2, Q3, Q4, Q5, Q6, Q7, Q8, Q9, Q10, Q11, Q12, Q13, Q14, Q15, Q16, Q17, Q18, Q19, Q20, Q21, Q22, Q23, Q24, Q25, Q26, Q27, Q28, Q29, Q30, Q31, Q32, Q33, Q34, Q35, Q36, Q37, Q38, Q39, Q40, Q41, Q42, Q43, Q44, Q45, Q46, Q47, Q48, Q49, Q50, Q51, Q52, Q53, Q54, Q55]), "depth" : 4.44 * mm, "offsetDistance" : 25.4 * mm});
        }
    });
